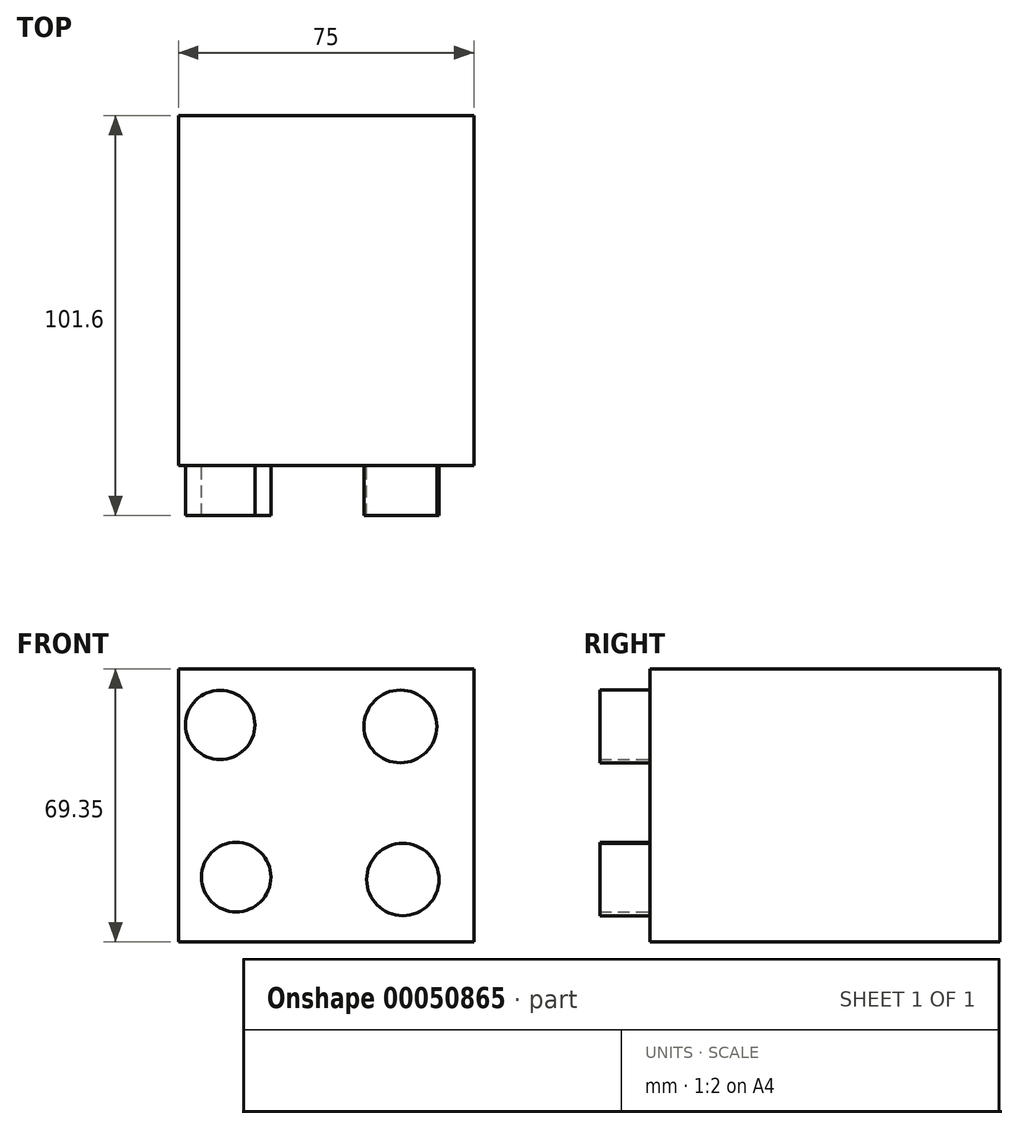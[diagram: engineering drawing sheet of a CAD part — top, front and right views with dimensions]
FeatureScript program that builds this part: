
annotation { "Feature Type Name" : "Feature", "Feature Type Description" : "" }
export const myFeature = defineFeature(function(context is Context, id is Id, definition is map)
    precondition{}
    {
        {
            var Q0;
            Q0=qCreatedBy(makeId("Front.planeOp"),FACE);
            var sketch = newSketch(context, id + "F0", { "sketchPlane" : qUnion([Q0])});
            skLineSegment(sketch, "E0.bottom", {"start": v(-75, 62.4) * mm, "end": v(0, 62.4) * mm});
            skLineSegment(sketch, "E0.top", {"start": v(-75, -6.94) * mm, "end": v(0, -6.94) * mm});
            skLineSegment(sketch, "E0.left", {"start": v(-75, 62.4) * mm, "end": v(-75, -6.94) * mm});
            skLineSegment(sketch, "E0.right", {"start": v(0, 62.4) * mm, "end": v(0, -6.94) * mm});
            skSolve(sketch);
        }
        {
            var Q0;
            Q0=makeQuery(id+"F0.imprint","IMPRINT",FACE,{"disambiguationData":[TD([[makeQuery(id+"F0.imprint","IMPRINT",EDGE,{"derivedFrom":sQuery(id+"F0.wireOp",EDGE,"E0.bottom")}),-1.0]])]});
            extrude(context, id + "F1", {"entities" : qUnion([Q0]), "depth" : 76.2 * mm});
        }
        {
            var Q0;
            Q0=makeQuery(id+"F1.opExtrude","CAP_FACE",FACE,{"disambiguationData":[OSD([sQuery(id+"F0.wireOp",EDGE,"E0.bottom"),sQuery(id+"F0.wireOp",EDGE,"E0.top"),sQuery(id+"F0.wireOp",EDGE,"E0.left"),sQuery(id+"F0.wireOp",EDGE,"E0.right")])],"isStart":false});
            var sketch = newSketch(context, id + "F2", { "sketchPlane" : qUnion([Q0])});
            skCircle(sketch, "E1", {"center": v(-60.77, 47.4) * mm, "radius": 9.12 * mm});
            skCircle(sketch, "E2", {"center": v(-21.67, 46.59) * mm, "radius": 9.68 * mm});
            skCircle(sketch, "E3", {"center": v(-58.13, 13.57) * mm, "radius": 9.63 * mm});
            skCircle(sketch, "E4", {"center": v(-20.46, 14.58) * mm, "radius": 9.93 * mm});
            skSolve(sketch);
        }
        {
            var Q0;
            Q0=makeQuery(id+"F2.imprint","IMPRINT",FACE,{"disambiguationData":[TD([[makeQuery(id+"F2.imprint","IMPRINT",EDGE,{"derivedFrom":sQuery(id+"F2.wireOp",EDGE,"E1")}),1.0]])]});
            extrude(context, id + "F3", {"entities" : qUnion([Q0]), "operationType" : NewBodyOperationType.ADD, "depth" : 12.7 * mm});
        }
        {
            var Q0;
            Q0=makeQuery(id+"F1.opExtrude","CAP_FACE",FACE,{"disambiguationData":[OSD([sQuery(id+"F0.wireOp",EDGE,"E0.bottom"),sQuery(id+"F0.wireOp",EDGE,"E0.top"),sQuery(id+"F0.wireOp",EDGE,"E0.left"),sQuery(id+"F0.wireOp",EDGE,"E0.right")])],"isStart":false});
            extrude(context, id + "F4", {"entities" : qUnion([Q0]), "operationType" : NewBodyOperationType.ADD, "depth" : 12.7 * mm});
        }
        {
            var Q0;
            Q0=makeQuery(id+"F4.boolean.opBoolean","MERGE",FACE,{"derivedFrom":[makeQuery(id+"F3.opExtrude","CAP_FACE",FACE,{"disambiguationData":[OSD([sQuery(id+"F2.wireOp",EDGE,"E1")])],"isStart":false}),makeQuery(id+"F4.opExtrude","CAP_FACE",FACE,{"disambiguationData":[OSD([sQuery(id+"F0.wireOp",EDGE,"E0.bottom"),sQuery(id+"F0.wireOp",EDGE,"E0.top"),sQuery(id+"F0.wireOp",EDGE,"E0.left"),sQuery(id+"F0.wireOp",EDGE,"E0.right")])],"isStart":false})]});
            var sketch = newSketch(context, id + "F5", { "sketchPlane" : qUnion([Q0])});
            skCircle(sketch, "E5", {"center": v(-64.41, 48.2) * mm, "radius": 8.8 * mm});
            skCircle(sketch, "E6", {"center": v(-18.64, 47.8) * mm, "radius": 9.25 * mm});
            skCircle(sketch, "E7", {"center": v(-18.03, 8.91) * mm, "radius": 9.19 * mm});
            skCircle(sketch, "E8", {"center": v(-60.36, 9.52) * mm, "radius": 8.82 * mm});
            skSolve(sketch);
        }
        {
            var Q0;
            Q0=makeQuery(id+"F5.imprint","IMPRINT",FACE,{"disambiguationData":[TD([[makeQuery(id+"F5.imprint","IMPRINT",EDGE,{"derivedFrom":sQuery(id+"F5.wireOp",EDGE,"E5")}),1.0]])]});
            var Q1;
            Q1=makeQuery(id+"F5.imprint","IMPRINT",FACE,{"disambiguationData":[TD([[makeQuery(id+"F5.imprint","IMPRINT",EDGE,{"derivedFrom":sQuery(id+"F5.wireOp",EDGE,"E6")}),1.0]])]});
            var Q2;
            Q2=makeQuery(id+"F5.imprint","IMPRINT",FACE,{"disambiguationData":[TD([[makeQuery(id+"F5.imprint","IMPRINT",EDGE,{"derivedFrom":sQuery(id+"F5.wireOp",EDGE,"E7")}),1.0]])]});
            var Q3;
            Q3=makeQuery(id+"F5.imprint","IMPRINT",FACE,{"disambiguationData":[TD([[makeQuery(id+"F5.imprint","IMPRINT",EDGE,{"derivedFrom":sQuery(id+"F5.wireOp",EDGE,"E8")}),1.0]])]});
            extrude(context, id + "F6", {"entities" : qUnion([Q0, Q1, Q2, Q3]), "operationType" : NewBodyOperationType.ADD, "depth" : 12.7 * mm});
        }
    });
